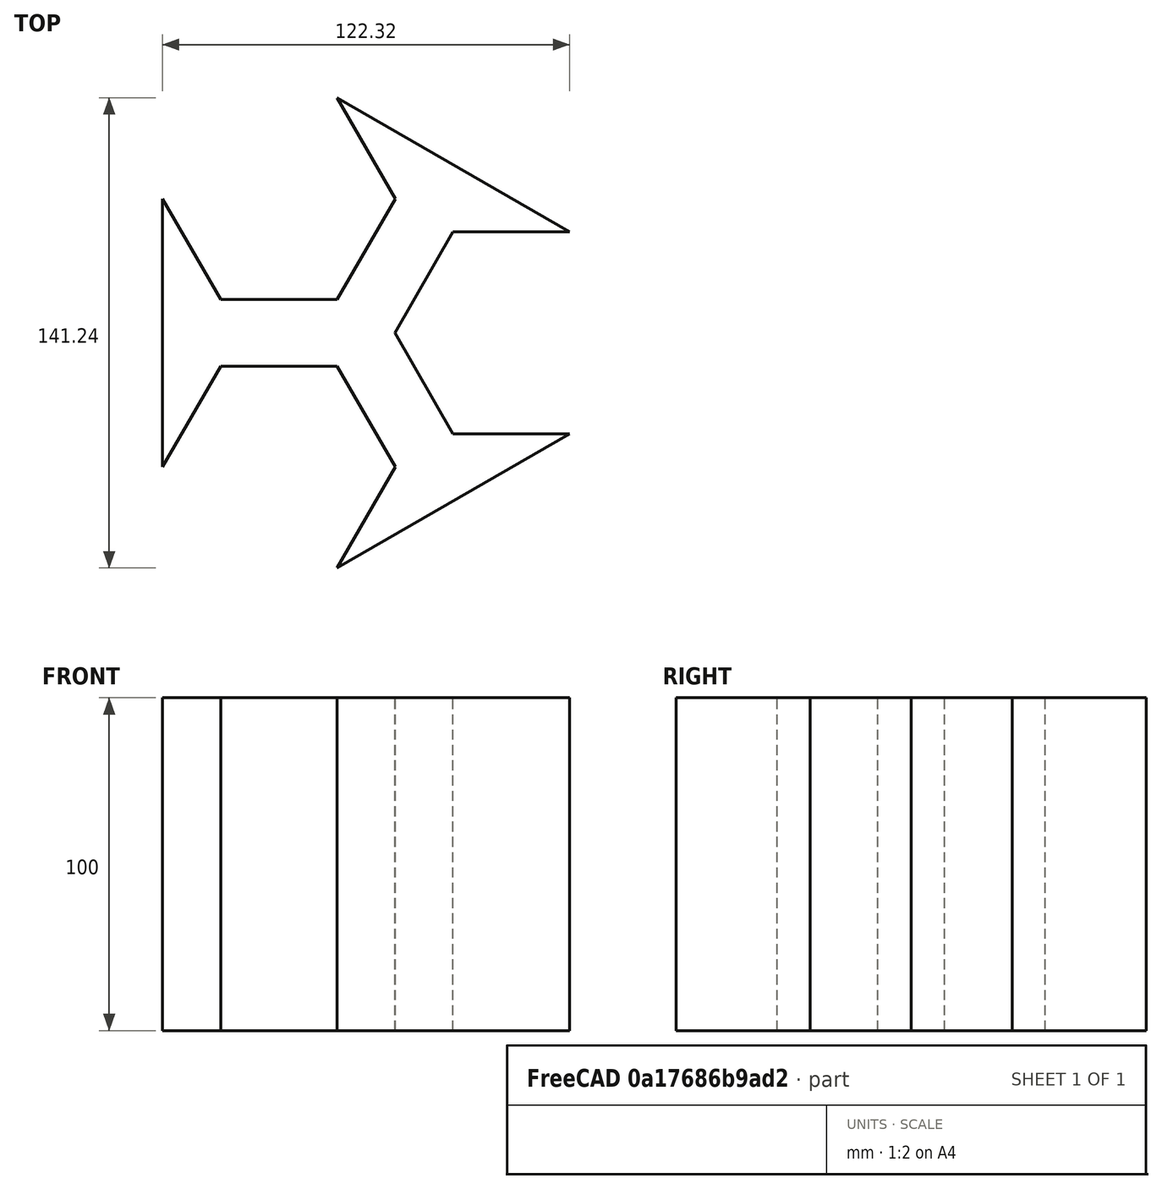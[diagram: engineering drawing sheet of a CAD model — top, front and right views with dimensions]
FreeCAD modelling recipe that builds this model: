
FCSTD DOCUMENT  (FreeCAD 0.22R38261 (Git))
Label: отцеп
License: All rights reserved
LicenseURL: https://en.wikipedia.org/wiki/All_rights_reserved
objects: Sketcher::SketchObject×1, PartDesign::Pad×1, PartDesign::Body×1, App::Part×1
note: 5 computed .brp shape members not serialized (recipe doc carries the construction recipe); baked Part::Feature solids carry a one-line shape summary decoded from their .brp

FEATURE [Sketcher::SketchObject] Sketch
  AttachmentSupport = -> [XY_Plane001]
  FullyConstrained = true
  MapMode = 5
  expr: Constraints[55] = .Constraints.MejduGaek
  expr: Constraints[56] = .Constraints.MejduGaek
  expr: Constraints[57] = .Constraints.MejduGaek
  expr: Constraints[58] = .Constraints.MejduGaek
  sketch-geometry (36):
    g0: LineSegment StartX=-35 StartY=9.99999 StartZ=0 EndX=-6.31364e-06 EndY=9.99999 EndZ=0
    g1: LineSegment StartX=-6.31364e-06 StartY=9.99999 StartZ=0 EndX=17.5 EndY=40.3109 EndZ=0
    g2: LineSegment StartX=17.5 StartY=40.3109 StartZ=0 EndX=-6.31364e-06 EndY=70.6218 EndZ=0
    g3: LineSegment StartX=-6.31364e-06 StartY=70.6218 StartZ=0 EndX=-35 EndY=70.6218 EndZ=0
    g4: LineSegment StartX=-35 StartY=70.6218 StartZ=0 EndX=-52.5 EndY=40.3109 EndZ=0
    g5: LineSegment StartX=-52.5 StartY=40.3109 StartZ=0 EndX=-35 EndY=9.99999 EndZ=0
    g6: Circle CenterX=-17.5 CenterY=40.3109 CenterZ=0 NormalX=0 NormalY=0 NormalZ=1 AngleXU=0 Radius=35
    g7: LineSegment StartX=69.8205 StartY=-30.3109 StartZ=0 EndX=87.3205 EndY=-3.6e-15 EndZ=0
    g8: LineSegment StartX=87.3205 StartY=-3.6e-15 StartZ=0 EndX=69.8205 EndY=30.3109 EndZ=0
    g9: LineSegment StartX=69.8205 StartY=30.3109 StartZ=0 EndX=34.8205 EndY=30.3109 EndZ=0
    g10: LineSegment StartX=34.8205 StartY=30.3109 StartZ=0 EndX=17.3205 EndY=0 EndZ=0
    g11: LineSegment StartX=17.3205 StartY=0 StartZ=0 EndX=34.8205 EndY=-30.3109 EndZ=0
    g12: LineSegment StartX=34.8205 StartY=-30.3109 StartZ=0 EndX=69.8205 EndY=-30.3109 EndZ=0
    g13: Circle CenterX=52.3205 CenterY=3.1e-15 CenterZ=0 NormalX=0 NormalY=0 NormalZ=1 AngleXU=0 Radius=35
    g14: LineSegment StartX=7.1e-15 StartY=-70.6218 StartZ=0 EndX=17.5 EndY=-40.3109 EndZ=0
    g15: LineSegment StartX=17.5 StartY=-40.3109 StartZ=0 EndX=0 EndY=-10 EndZ=0
    g16: LineSegment StartX=0 StartY=-10 StartZ=0 EndX=-35 EndY=-10 EndZ=0
    g17: LineSegment StartX=-35 StartY=-10 StartZ=0 EndX=-52.5 EndY=-40.3109 EndZ=0
    g18: LineSegment StartX=-52.5 StartY=-40.3109 StartZ=0 EndX=-35 EndY=-70.6218 EndZ=0
    g19: LineSegment StartX=-35 StartY=-70.6218 StartZ=0 EndX=7.1e-15 EndY=-70.6218 EndZ=0
    g20: Circle CenterX=-17.5 CenterY=-40.3109 CenterZ=0 NormalX=0 NormalY=0 NormalZ=1 AngleXU=0 Radius=35
    g21: LineSegment StartX=17.5 StartY=-40.3109 StartZ=0 EndX=0 EndY=-10 EndZ=0
    g22: LineSegment StartX=0 StartY=-10 StartZ=0 EndX=-35 EndY=-10 EndZ=0
    g23: LineSegment StartX=-35 StartY=9.99999 StartZ=0 EndX=-6.31364e-06 EndY=9.99999 EndZ=0
    g24: LineSegment StartX=-6.31364e-06 StartY=9.99999 StartZ=0 EndX=17.5 EndY=40.3109 EndZ=0
    g25: LineSegment StartX=17.3205 StartY=0 StartZ=0 EndX=34.8205 EndY=30.3109 EndZ=0
    g26: LineSegment StartX=17.3205 StartY=0 StartZ=0 EndX=34.8205 EndY=-30.3109 EndZ=0
    g27: LineSegment StartX=17.5 StartY=-40.3109 StartZ=0 EndX=7.1e-15 EndY=-70.6218 EndZ=0
    g28: LineSegment StartX=7.1e-15 StartY=-70.6218 StartZ=0 EndX=69.8205 EndY=-30.3109 EndZ=0
    g29: LineSegment StartX=34.8205 StartY=-30.3109 StartZ=0 EndX=69.8205 EndY=-30.3109 EndZ=0
    g30: LineSegment StartX=-35 StartY=-10 StartZ=0 EndX=-52.5 EndY=-40.3109 EndZ=0
    g31: LineSegment StartX=-35 StartY=9.99999 StartZ=0 EndX=-52.5 EndY=40.3109 EndZ=0
    g32: LineSegment StartX=34.8205 StartY=30.3109 StartZ=0 EndX=69.8205 EndY=30.3109 EndZ=0
    g33: LineSegment StartX=17.5 StartY=40.3109 StartZ=0 EndX=-6.31364e-06 EndY=70.6218 EndZ=0
    g34: LineSegment StartX=69.8205 StartY=30.3109 StartZ=0 EndX=-6.31364e-06 EndY=70.6218 EndZ=0
    g35: LineSegment StartX=-52.5 StartY=40.3109 StartZ=0 EndX=-52.5 EndY=-40.3109 EndZ=0
  constraints (81):
    c: Coincident(g0,g1)
    c: Coincident(g1,g2)
    c: Coincident(g2,g3)
    c: Coincident(g3,g4)
    c: Coincident(g4,g5)
    c: Coincident(g5,g0)
    c: Equal(g0, g1-g5) x5
    c: PointOnObject(g0,g6)
    c: PointOnObject(g1,g6)
    c: PointOnObject(g2,g6)
    c: PointOnObject(g3,g6)
    c: PointOnObject(g4,g6)
    c: PointOnObject(g5,g6)
    c: Distance(g5) = 35
    c: Coincident(g7,g8)
    c: Coincident(g8,g9)
    c: Coincident(g9,g10)
    c: Coincident(g10,g11)
    c: Coincident(g11,g12)
    c: Coincident(g12,g7)
    c: Equal(g7, g8-g12) x5
    c: PointOnObject(g7,g13)
    c: PointOnObject(g8,g13)
    c: PointOnObject(g9,g13)
    c: PointOnObject(g10,g13)
    c: PointOnObject(g11,g13)
    c: PointOnObject(g12,g13)
    c: Distance(g10) = 35
    c: Coincident(g14,g15)
    c: Coincident(g15,g16)
    c: Coincident(g16,g17)
    c: Coincident(g17,g18)
    c: Coincident(g18,g19)
    c: Coincident(g19,g14)
    c: Equal(g14, g15-g19) x5
    c: PointOnObject(g14,g20)
    c: PointOnObject(g15,g20)
    c: PointOnObject(g16,g20)
    c: PointOnObject(g17,g20)
    c: PointOnObject(g18,g20)
    c: PointOnObject(g19,g20)
    c: Distance(g15) = 35
    c: Distance(g16,g0) = 20  'MejduGaek'
    c: Distance(g15,g0) = 20
    c: Distance(g10,g0) = 20
    c: Distance(g9,g1) = 20
    c: Distance(g14,g11) = 20
    c: PointOnObject(g15,g-2)
    c: PointOnObject(g10,g-1)
    c: Parallel(g-1,g0)
    c: Coincident(g21,g14)
    c: Coincident(g21,g15)
    c: Coincident(g22,g15)
    c: Coincident(g22,g16)
    c: Coincident(g23,g0)
    c: Coincident(g23,g0)
    c: Coincident(g24,g0)
    c: Coincident(g24,g1)
    c: Coincident(g25,g10)
    c: Coincident(g25,g9)
    c: Coincident(g26,g10)
    c: Coincident(g26,g11)
    c: Coincident(g27,g14)
    c: Coincident(g27,g14)
    c: Coincident(g28,g14)
    c: Coincident(g28,g7)
    c: Tangent(g28,g13)
    c: Coincident(g29,g11)
    c: Coincident(g29,g7)
    c: Coincident(g30,g16)
    c: Coincident(g30,g17)
    c: Coincident(g31,g0)
    c: Coincident(g31,g4)
    c: Coincident(g32,g9)
    c: Coincident(g32,g8)
    c: Coincident(g33,g1)
    c: Coincident(g33,g2)
    c: Coincident(g34,g8)
    c: Coincident(g34,g2)
    c: Coincident(g35,g4)
    c: Coincident(g35,g17)
FEATURE [PartDesign::Pad] Pad
  Direction = (0,0,1)
  Length = 100
  Length2 = 10
  Profile = -> Sketch
  ReferenceAxis = -> Sketch [N_Axis]
  Suppressed = false
  Type = 0
FEATURE [PartDesign::Body] Body
  AllowCompound = false
  Group = -> [Sketch,Pad]
  Origin = -> Origin001
  Tip = -> Pad
FEATURE [App::Part] Part
  Group = -> [Body]
  Origin = -> Origin
